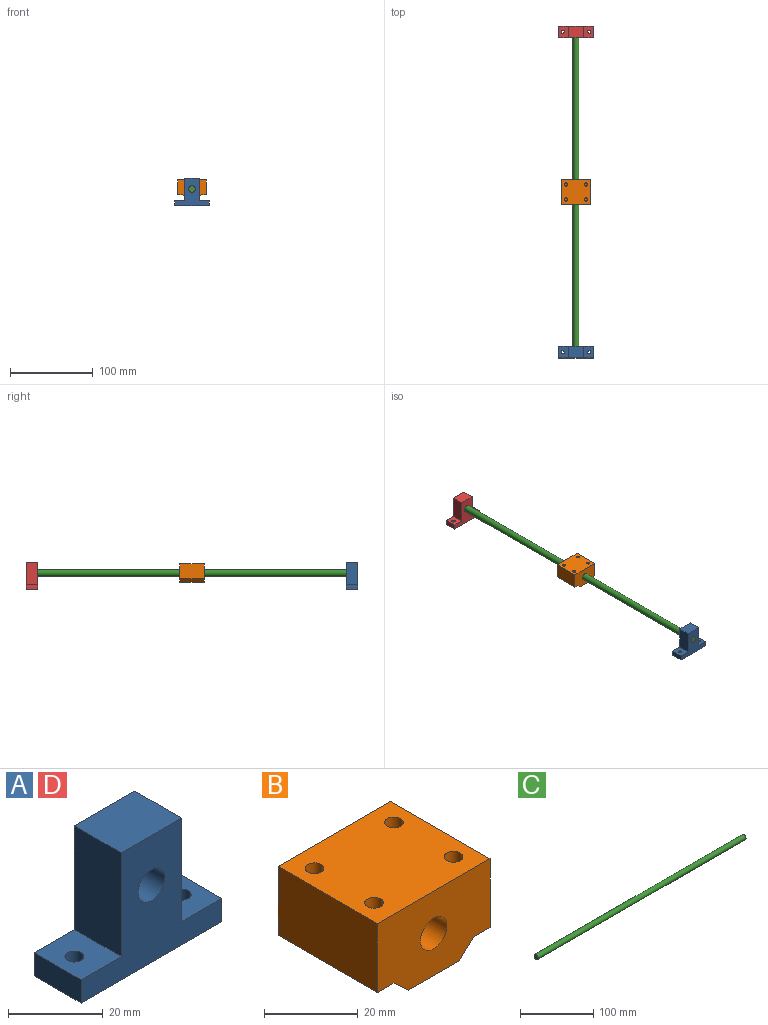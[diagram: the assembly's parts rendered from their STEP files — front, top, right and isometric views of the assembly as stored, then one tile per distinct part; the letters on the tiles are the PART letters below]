
ASSEMBLY  parts=4 mates=3
PART A: 13 faces, bbox 42x14x32.8 mm
  f0: plane 18x14mm, normal (0,0,1), area 252mm2, adj f1,f8,f9,f10
  f1: plane 26.8x14mm, normal (-1,0,0), area 375.2mm2, adj f0,f2,f9,f10
  f2: plane 14x12mm, normal (0,0,1), area 155.4mm2, adj f1,f3,f9,f10,f12
  f3: plane 14x6mm, normal (-1,0,0), area 84mm2, adj f2,f4,f9,f10
  f4: plane 42x14mm, normal (0,0,-1), area 562.9mm2, adj f3,f5,f9,f10,f11,f12
  f5: plane 14x6mm, normal (1,0,0), area 84mm2, adj f4,f6,f9,f10
  f6: plane 14x12mm, normal (0,0,1), area 155.4mm2, adj f5,f8,f9,f10,f11
  f7: cylinder r=4mm len=14mm, axis (0,1,0), area 351.9mm2, adj f9,f10
  f8: plane 26.8x14mm, normal (1,0,0), area 375.2mm2, adj f0,f6,f9,f10
  f9: plane 42x32.8mm, normal (0,-1,0), area 684.1mm2, adj f0,f1,f2,f3,f4,f5,f6,f7
  f10: plane 42x32.8mm, normal (0,1,0), area 684.1mm2, adj f0,f1,f2,f3,f4,f5,f6,f7
  f11: cylinder r=2mm len=6mm, axis (0,0,-1), area 75.4mm2, adj f4,f6
  f12: cylinder r=2mm len=6mm, axis (0,0,-1), area 75.4mm2, adj f2,f4
PART B: 19 faces, bbox 34x30x22 mm
  f0: plane 30x5.02mm, normal (0,0,-1), area 150.6mm2, adj f1,f7,f9,f10
  f1: plane 30x4.28mm, normal (-0.68,0,-0.73), area 175.7mm2, adj f0,f2,f9,f10
  f2: plane 30x15.4mm, normal (0,0,-1), area 462.1mm2, adj f1,f3,f9,f10
  f3: plane 30x4.28mm, normal (0.68,0,-0.73), area 175.7mm2, adj f2,f4,f9,f10
  f4: plane 30x5.02mm, normal (0,0,-1), area 150.6mm2, adj f3,f5,f9,f10
  f5: plane 30x18mm, normal (1,0,0), area 540mm2, adj f4,f6,f9,f10
  f6: plane 34x30mm, normal (0,0,1), area 969.7mm2, adj f5,f7,f9,f10,f12,f14,f16,f18
  f7: plane 30x18mm, normal (-1,0,0), area 540mm2, adj f0,f6,f9,f10
  f8: cylinder r=4mm len=30mm, axis (0,1,0), area 754mm2, adj f9,f10
  f9: plane 34x22mm, normal (0,-1,0), area 640.5mm2, adj f0,f1,f2,f3,f4,f5,f6,f7
  f10: plane 34x22mm, normal (0,1,0), area 640.5mm2, adj f0,f1,f2,f3,f4,f5,f6,f7
  f11: cone r=0mm half-angle=59deg, axis (0,0,1), area 14.7mm2, adj f12
  f12: cylinder r=2mm len=12mm, axis (0,0,1), area 150.8mm2, adj f6,f11
  f13: cone r=0mm half-angle=59deg, axis (0,0,1), area 14.7mm2, adj f14
  f14: cylinder r=2mm len=12mm, axis (0,0,1), area 150.8mm2, adj f6,f13
  f15: cone r=0mm half-angle=59deg, axis (0,0,1), area 14.7mm2, adj f16
  f16: cylinder r=2mm len=12mm, axis (0,0,1), area 150.8mm2, adj f6,f15
  f17: cone r=0mm half-angle=59deg, axis (0,0,1), area 14.7mm2, adj f18
  f18: cylinder r=2mm len=12mm, axis (0,0,1), area 150.8mm2, adj f6,f17
PART C: 3 faces, bbox 400x8x8 mm
  f0: cylinder r=4mm len=400mm, axis (-1,0,0), area 10053.1mm2, adj f1,f2
  f1: plane 8x8mm, normal (1,0,0), area 50.3mm2, adj f0
  f2: plane 8x8mm, normal (-1,0,0), area 50.3mm2, adj f0
PART D: same geometry as A
PLACE A at identity fixed
PLACE B t=(0,201,20)mm
PLACE C rot(axis=(-0.58,0.58,-0.58),120deg) t=(-64.79,186,67.36)mm
PLACE D t=(0,386,0)mm
MATE fastened C.f0 <-> A.f7  axis (0,-1,0) through (0,-14,20)mm
MATE slider B.f8 <-> C.f0  axis (0,1,0) through (0,186,20)mm
MATE fastened D.f7 <-> C.f0  axis (0,1,0) through (0,386,20)mm
